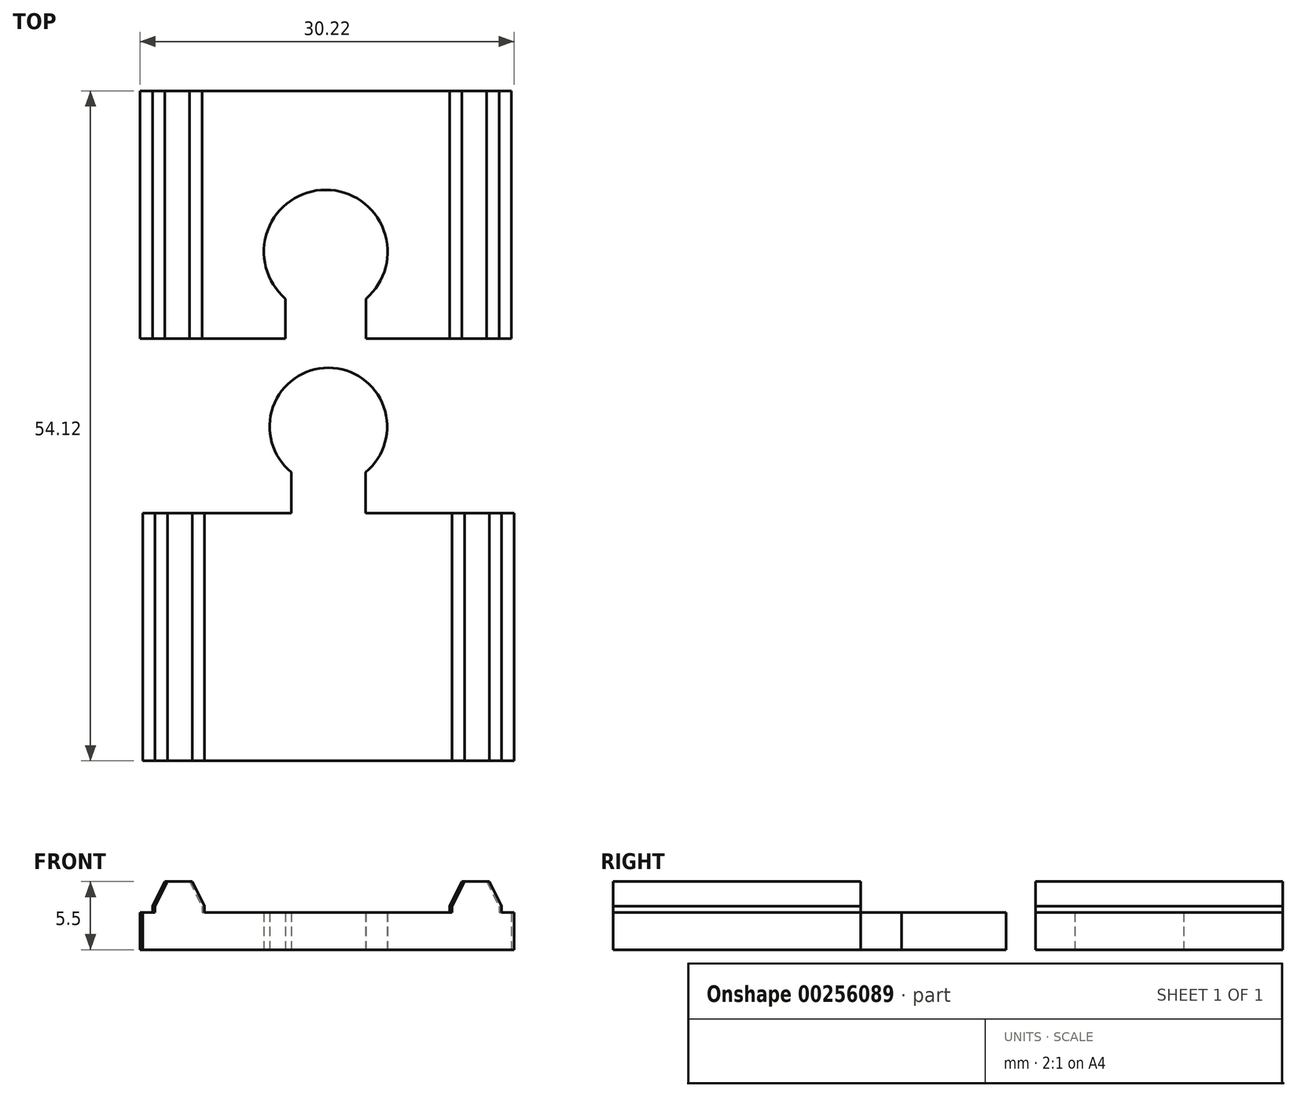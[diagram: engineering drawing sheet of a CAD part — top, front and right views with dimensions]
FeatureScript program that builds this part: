
annotation { "Feature Type Name" : "Feature", "Feature Type Description" : "" }
export const myFeature = defineFeature(function(context is Context, id is Id, definition is map)
    precondition{}
    {
        {
            var Q0;
            Q0=qCreatedBy(makeId("Top.planeOp"),FACE);
            var sketch = newSketch(context, id + "F0", { "sketchPlane" : qUnion([Q0])});
            skLineSegment(sketch, "E0.bottom", {"start": v(-27.13, -41.38) * mm, "end": v(2.87, -41.38) * mm});
            skLineSegment(sketch, "E0.top", {"start": v(-27.13, -21.38) * mm, "end": v(2.87, -21.38) * mm});
            skLineSegment(sketch, "E0.left", {"start": v(-27.13, -41.38) * mm, "end": v(-27.13, -21.38) * mm});
            skLineSegment(sketch, "E0.right", {"start": v(2.87, -41.38) * mm, "end": v(2.87, -21.38) * mm});
            skLineSegment(sketch, "E1", {"start": v(-12.13, -21.38) * mm, "end": v(-12.13, -14.38) * mm});
            skCircle(sketch, "E2", {"center": v(-12.13, -14.38) * mm, "radius": 4.75 * mm});
            skLineSegment(sketch, "E3", {"start": v(-9.13, -21.38) * mm, "end": v(-9.13, -18.06) * mm});
            skLineSegment(sketch, "E4", {"start": v(-15.13, -21.38) * mm, "end": v(-15.13, -18.06) * mm});
            skSolve(sketch);
        }
        {
            var Q0;
            Q0=makeQuery(id+"F0.imprint","IMPRINT",FACE,{"disambiguationData":[TD([[makeQuery(id+"F0.imprint","IMPRINT",EDGE,{"derivedFrom":sQuery(id+"F0.wireOp",EDGE,"E0.bottom")}),1.0]])]});
            var Q1;
            {var subQ3=sQuery(id+"F0.wireOp",EDGE,"E4");Q1=makeQuery(id+"F0.imprint","IMPRINT",FACE,{"disambiguationData":[TD([[makeQuery(id+"F0.imprint","IMPRINT",EDGE,{"derivedFrom":subQ3}),-1.0]])]});}
            var Q2;
            {var subQ3=sQuery(id+"F0.wireOp",EDGE,"E3");Q2=makeQuery(id+"F0.imprint","IMPRINT",FACE,{"disambiguationData":[TD([[makeQuery(id+"F0.imprint","IMPRINT",EDGE,{"derivedFrom":subQ3}),1.0]])]});}
            var Q3;
            {var subQ0=sQuery(id+"F0.wireOp",EDGE,"E2");var subQ1=makeQuery(id+"F0.imprint","INTERSECT",VERTEX,{"derivedFrom":[subQ0,sQuery(id+"F0.wireOp",EDGE,"E4")]});Q3=makeQuery(id+"F0.imprint","IMPRINT",FACE,{"disambiguationData":[TD([[makeQuery(id+"F0.imprint","IMPRINT",EDGE,{"disambiguationData":[TD([[subQ1,-1.0]])],"derivedFrom":subQ0}),1.0]])]});}
            extrude(context, id + "F1", {"entities" : qUnion([Q0, Q1, Q2, Q3]), "depth" : 3 * mm});
        }
        {
            var Q0;
            Q0=makeQuery(id+"F1.opExtrude","CAP_FACE",FACE,{"disambiguationData":[OSD([sQuery(id+"F0.wireOp",EDGE,"E0.bottom"),sQuery(id+"F0.wireOp",EDGE,"E0.top"),sQuery(id+"F0.wireOp",EDGE,"E0.left"),sQuery(id+"F0.wireOp",EDGE,"E0.right"),sQuery(id+"F0.wireOp",EDGE,"E2"),sQuery(id+"F0.wireOp",EDGE,"E3"),sQuery(id+"F0.wireOp",EDGE,"E4")])],"isStart":false});
            var sketch = newSketch(context, id + "F2", { "sketchPlane" : qUnion([Q0])});
            skLineSegment(sketch, "E5", {"start": v(-12.13, -41.38) * mm, "end": v(-12.13, -14.38) * mm});
            skLineSegment(sketch, "E6", {"start": v(-22.13, -41.38) * mm, "end": v(-22.13, -21.38) * mm});
            skLineSegment(sketch, "E7", {"start": v(-2.13, -41.38) * mm, "end": v(-2.13, -21.38) * mm});
            skLineSegment(sketch, "E8", {"start": v(-26.13, -41.38) * mm, "end": v(-26.13, -21.38) * mm});
            skLineSegment(sketch, "E9", {"start": v(1.87, -41.38) * mm, "end": v(1.87, -21.38) * mm});
            skSolve(sketch);
        }
        {
            var Q0;
            {var subQ0=sQuery(id+"F2.wireOp",EDGE,"E6");Q0=makeQuery(id+"F2.imprint","IMPRINT",FACE,{"disambiguationData":[TD([[makeQuery(id+"F2.imprint","IMPRINT",EDGE,{"derivedFrom":subQ0}),1.0]])]});}
            var Q1;
            {var subQ0=sQuery(id+"F2.wireOp",EDGE,"E7");Q1=makeQuery(id+"F2.imprint","IMPRINT",FACE,{"disambiguationData":[TD([[makeQuery(id+"F2.imprint","IMPRINT",EDGE,{"derivedFrom":subQ0}),-1.0]])]});}
            extrude(context, id + "F3", {"entities" : qUnion([Q0, Q1]), "operationType" : NewBodyOperationType.ADD, "depth" : 2.5 * mm});
        }
        {
            var Q0;
            Q0=makeQuery(id+"F3.opExtrude","CAP_EDGE",EDGE,{"disambiguationData":[OSD([sQuery(id+"F2.wireOp",EDGE,"E6")])],"isStart":false});
            var Q1;
            Q1=makeQuery(id+"F3.opExtrude","CAP_EDGE",EDGE,{"disambiguationData":[OSD([sQuery(id+"F2.wireOp",EDGE,"E8")])],"isStart":false});
            chamfer(context, id + "F4", {"entities" : qUnion([Q0, Q1]), "chamferType" : ChamferType.TWO_OFFSETS, "width1" : 1 ^ 5 * mm, "oppositeDirection" : false, "width2" : 2 * mm, "tangentPropagation" : true});
        }
        {
            var Q0;
            Q0=makeQuery(id+"F3.opExtrude","CAP_EDGE",EDGE,{"disambiguationData":[OSD([sQuery(id+"F2.wireOp",EDGE,"E7")])],"isStart":false});
            var Q1;
            Q1=makeQuery(id+"F3.opExtrude","CAP_EDGE",EDGE,{"disambiguationData":[OSD([sQuery(id+"F2.wireOp",EDGE,"E9")])],"isStart":false});
            chamfer(context, id + "F5", {"entities" : qUnion([Q0, Q1]), "chamferType" : ChamferType.TWO_OFFSETS, "width1" : 2 * mm, "oppositeDirection" : false, "width2" : 1 * mm, "tangentPropagation" : true});
        }
        {
            var Q0;
            Q0=qCreatedBy(makeId("Top.planeOp"),FACE);
            var sketch = newSketch(context, id + "F6", { "sketchPlane" : qUnion([Q0])});
            skLineSegment(sketch, "E10.bottom", {"start": v(-27.35, -7.26) * mm, "end": v(2.65, -7.26) * mm});
            skLineSegment(sketch, "E10.top", {"start": v(-27.35, 12.74) * mm, "end": v(2.65, 12.74) * mm});
            skLineSegment(sketch, "E10.left", {"start": v(-27.35, -7.26) * mm, "end": v(-27.35, 12.74) * mm});
            skLineSegment(sketch, "E10.right", {"start": v(2.65, -7.26) * mm, "end": v(2.65, 12.74) * mm});
            skLineSegment(sketch, "E11", {"start": v(-12.35, -7.26) * mm, "end": v(-12.35, 12.74) * mm, "construction": true});
            skCircle(sketch, "E12", {"center": v(-12.35, -0.26) * mm, "radius": 5 * mm});
            skLineSegment(sketch, "E13", {"start": v(-15.6, -7.26) * mm, "end": v(-15.6, -4.06) * mm});
            skLineSegment(sketch, "E14", {"start": v(-9.1, -7.26) * mm, "end": v(-9.1, -4.06) * mm});
            skSolve(sketch);
        }
        {
            var Q0;
            Q0=makeQuery(id+"F6.imprint","IMPRINT",FACE,{"disambiguationData":[TD([[makeQuery(id+"F6.imprint","IMPRINT",EDGE,{"derivedFrom":sQuery(id+"F6.wireOp",EDGE,"E10.top")}),-1.0]])]});
            extrude(context, id + "F7", {"entities" : qUnion([Q0]), "depth" : 3 * mm});
        }
        {
            var Q0;
            Q0=makeQuery(id+"F7.opExtrude","CAP_FACE",FACE,{"disambiguationData":[OSD([sQuery(id+"F6.wireOp",EDGE,"E10.bottom"),sQuery(id+"F6.wireOp",EDGE,"E10.top"),sQuery(id+"F6.wireOp",EDGE,"E10.left"),sQuery(id+"F6.wireOp",EDGE,"E10.right"),sQuery(id+"F6.wireOp",EDGE,"E12"),sQuery(id+"F6.wireOp",EDGE,"E13"),sQuery(id+"F6.wireOp",EDGE,"E14")])],"isStart":false});
            var sketch = newSketch(context, id + "F8", { "sketchPlane" : qUnion([Q0])});
            skLineSegment(sketch, "E15", {"start": v(-22.35, -7.26) * mm, "end": v(-22.35, 12.74) * mm});
            skLineSegment(sketch, "E16", {"start": v(-26.35, -7.26) * mm, "end": v(-26.35, 12.74) * mm});
            skLineSegment(sketch, "E17", {"start": v(-2.35, 12.74) * mm, "end": v(-2.35, -7.26) * mm});
            skLineSegment(sketch, "E18", {"start": v(1.65, 12.74) * mm, "end": v(1.65, -7.26) * mm});
            skSolve(sketch);
        }
        {
            var Q0;
            {var subQ0=sQuery(id+"F8.wireOp",EDGE,"E15");Q0=makeQuery(id+"F8.imprint","IMPRINT",FACE,{"disambiguationData":[TD([[makeQuery(id+"F8.imprint","IMPRINT",EDGE,{"derivedFrom":subQ0}),1.0]])]});}
            var Q1;
            {var subQ0=sQuery(id+"F8.wireOp",EDGE,"E17");Q1=makeQuery(id+"F8.imprint","IMPRINT",FACE,{"disambiguationData":[TD([[makeQuery(id+"F8.imprint","IMPRINT",EDGE,{"derivedFrom":subQ0}),1.0]])]});}
            extrude(context, id + "F9", {"entities" : qUnion([Q0, Q1]), "operationType" : NewBodyOperationType.ADD, "depth" : 2.5 * mm});
        }
        {
            var Q0;
            Q0=makeQuery(id+"F9.opExtrude","CAP_EDGE",EDGE,{"disambiguationData":[OSD([sQuery(id+"F8.wireOp",EDGE,"E15")])],"isStart":false});
            var Q1;
            Q1=makeQuery(id+"F9.opExtrude","CAP_EDGE",EDGE,{"disambiguationData":[OSD([sQuery(id+"F8.wireOp",EDGE,"E16")])],"isStart":false});
            chamfer(context, id + "F10", {"entities" : qUnion([Q0, Q1]), "chamferType" : ChamferType.TWO_OFFSETS, "width1" : 1 * mm, "oppositeDirection" : false, "width2" : 2 * mm, "tangentPropagation" : true});
        }
        {
            var Q0;
            Q0=makeQuery(id+"F9.opExtrude","CAP_EDGE",EDGE,{"disambiguationData":[OSD([sQuery(id+"F8.wireOp",EDGE,"E18")])],"isStart":false});
            var Q1;
            Q1=makeQuery(id+"F9.opExtrude","CAP_EDGE",EDGE,{"disambiguationData":[OSD([sQuery(id+"F8.wireOp",EDGE,"E17")])],"isStart":false});
            chamfer(context, id + "F11", {"entities" : qUnion([Q0, Q1]), "chamferType" : ChamferType.TWO_OFFSETS, "width1" : 2 * mm, "oppositeDirection" : false, "width2" : 1 * mm, "tangentPropagation" : true});
        }
    });
